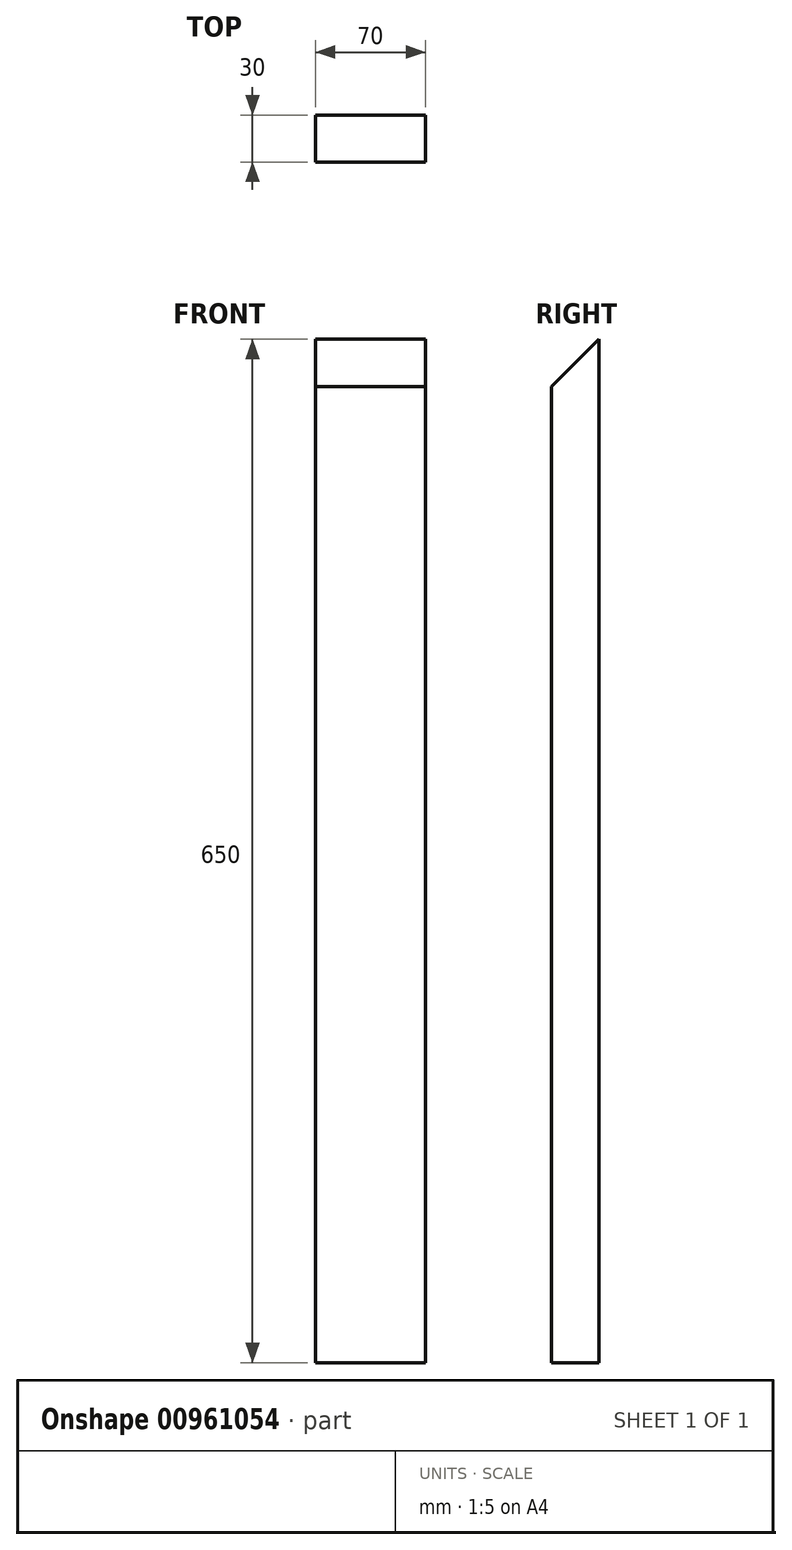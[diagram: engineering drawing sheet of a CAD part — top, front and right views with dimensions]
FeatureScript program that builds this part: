
annotation { "Feature Type Name" : "Feature", "Feature Type Description" : "" }
export const myFeature = defineFeature(function(context is Context, id is Id, definition is map)
    precondition{}
    {
        {
            var Q0;
            Q0=qCreatedBy(makeId("Right.planeOp"),FACE);
            var sketch = newSketch(context, id + "F0", { "sketchPlane" : qUnion([Q0])});
            skLineSegment(sketch, "E0.top", {"start": v(-22.12, -650) * mm, "end": v(7.88, -650) * mm});
            skLineSegment(sketch, "E0.left", {"start": v(-22.12, -30) * mm, "end": v(-22.12, -650) * mm});
            skLineSegment(sketch, "E0.right", {"start": v(7.88, 0) * mm, "end": v(7.88, -650) * mm});
            skLineSegment(sketch, "E1", {"start": v(7.88, 0) * mm, "end": v(-22.12, -30) * mm});
            skPoint(sketch, "E2.orphan", {"position": v(-22.12, 0) * mm});
            skSolve(sketch);
        }
        {
            var Q0;
            Q0=makeQuery(id+"F0.imprint","IMPRINT",FACE,{"disambiguationData":[TD([[makeQuery(id+"F0.imprint","IMPRINT",EDGE,{"derivedFrom":sQuery(id+"F0.wireOp",EDGE,"E0.top")}),1.0]])]});
            extrude(context, id + "F1", {"entities" : qUnion([Q0]), "endBound" : BoundingType.SYMMETRIC, "depth" : 70 * mm, "offsetDistance" : 25 * mm});
        }
    });
